# Revit family: CAME_Турникет_Калитка_WINGGL_Автоматическая
name_source: partatom
category: Специальное оборудование
units: mm (PartAtom-declared; Revit-internal decimal feet)

## family parameters
Всегда вертикально = Да
На основе рабочей плоскости = Нет
Общий = Нет
При загрузке вырезать с полостями = Нет
Размер круглого соединителя = Использовать диаметр
Тип детали = Нормальный
Точка расчета площади = Нет

## types (3) — shared parameters
ADSK_URL документации изделия = https://camerussia.com
ADSK_URL страницы изделия = https://camerussia.com
ADSK_Версия Revit = 2019
ADSK_Версия семейства = 1.0
ADSK_Группирование = WING
ADSK_Единица измерения = шт.
ADSK_Завод-изготовитель = CAME
ADSK_Классификация нагрузок = Прочее
ADSK_Код изделия = Код КСР 26.30.50.119.61.2.07.09
ADSK_Количество = 1
ADSK_Количество фаз = 1
ADSK_Коэффициент мощности = 0.96
ADSK_Напряжение = 230 В
ADSK_Номинальная мощность = 65 Вт
ADSK_Обозначение = ТУ 26.30.50-001-89603926-2021
ADSK_Полная мощность = 68 В·А
ADSK_Размер_Диаметр = 230 мм
BL_BIM library = https://bimlib.pro
CAME_Время открывания (с) = 2.5
CAME_Диапазон рабочих температур (°C) = -20 ÷ +68
CAME_Интенсивность использования (%) = ИНТЕНСИВНОЕ
CAME_Класс защиты (IP) = 44
CAME_Напряжение электропитания двигателя (В) = 24 В
CAME_Тип механизма турникета = моторизованный
URL = https://camerussia.com
Группа модели = Турникеты
Изготовитель = CAME

## per-type parameters (varying)
| type | ADSK_Марка | ADSK_Масса | ADSK_Масса_Текст | ADSK_Наименование | ADSK_Наименование краткое | ADSK_Размер_Высота | ADSK_Размер_Ширина | Описание | Полноростовая | Полуростовая | Ширина створки |
| 550 | АРТ:001PSWNG4GL1 | 50 | 50 | Турникет-калитка моторизованная WING GL со створкой из закаленного стекла 550 мм | Турникет-калитка WING GL 550 мм | 1030 мм | 780 мм | Турникет-калитка автоматическая. Корпус из нержавеющей стали AISI 304. Оснащена платой управления и светодиодным индикатором. Сервопозиционный электропривод створки с определением препятствий и разблокировкой при отключении электропитания. Створка из 10 мм закаленного стекла 550 мм (высота установленной створки 930). Встроенный блок питания. | Нет | Да | 550 мм |
| 900 | АРТ:001PSWNG4GLA1 | 50 | 50 | Турникет-калитка моторизованная WING GL со створкой из закаленного стекла 900 мм | Турникет-калитка WING GL 900 мм | 1030 мм | 1130 мм | Турникет-калитка автоматическая. Корпус из нержавеющей стали AISI 304. Оснащена платой управления и светодиодным индикатором. Сервопозиционный электропривод створки с определением препятствий и разблокировкой при отключении электропитания. Створка из 10 мм закаленного стекла 900 мм (высота установленной створки 930). Встроенный блок питания. | Нет | Да | 900 мм |
| 900 полноростовая | АРТ:001PSWNG4GLA2 | 90 | 90 | Турникет-калитка полноростовая моторизованная WING GL со створкой из закаленного стекла 900 мм | Турникет-калитка WING GL 900 мм полноростовая | 1500 мм | 1130 мм | Турникет-калитка полноростовая автоматическая. Корпус из нержавеющей стали AISI 304 Оснащена платой управления и светодиодным индикатором. Сервопозиционный электропривод створки с определением препятствий и разблокировкой при отключении электропитания. Створка из 10 мм закаленного стекла 900 мм (высота установленной створки 1500). Встроенный блок питания. | Да | Нет | 900 мм |
